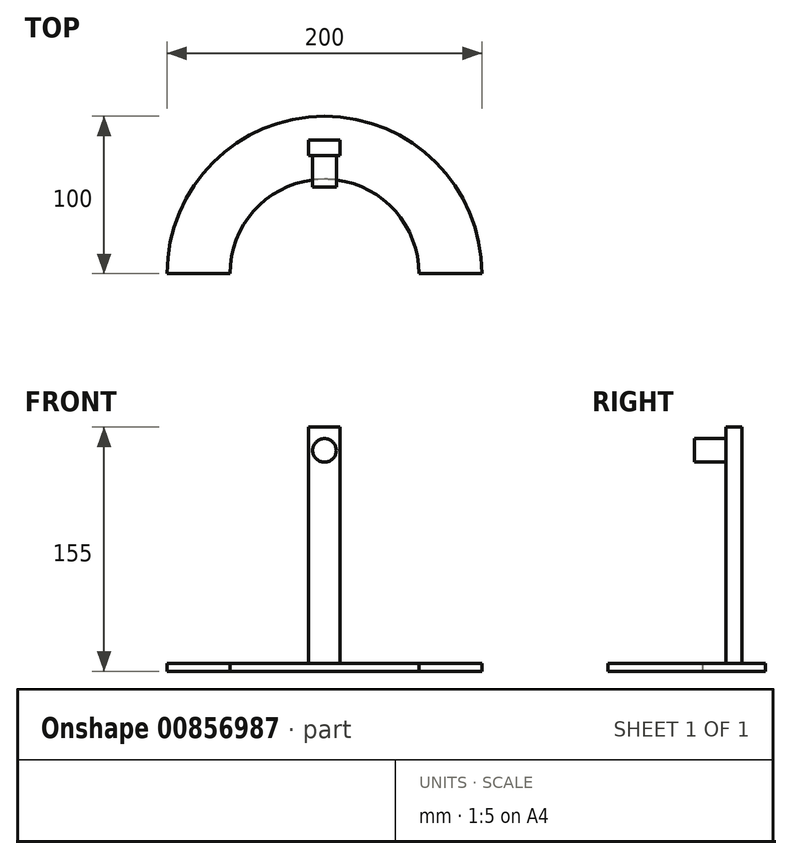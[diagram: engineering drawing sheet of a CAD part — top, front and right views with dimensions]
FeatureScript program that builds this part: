
annotation { "Feature Type Name" : "Feature", "Feature Type Description" : "" }
export const myFeature = defineFeature(function(context is Context, id is Id, definition is map)
    precondition{}
    {
        {
            var Q0;
            Q0=qCreatedBy(makeId("Top.planeOp"),FACE);
            var sketch = newSketch(context, id + "F0", { "sketchPlane" : qUnion([Q0])});
            skArc(sketch, "E0", {"start": v(100, 0) * mm, "mid": v(0, 100) * mm, "end": v(-100, 0) * mm});
            skLineSegment(sketch, "E1", {"start": v(-100, 0) * mm, "end": v(-60, 0) * mm});
            skPoint(sketch, "E2.orphan", {"position": v(-105.17, 0) * mm});
            skArc(sketch, "E3", {"start": v(60, 0) * mm, "mid": v(0, 60) * mm, "end": v(-60, 0) * mm});
            skLineSegment(sketch, "E4.trimOffspring", {"start": v(60, 0) * mm, "end": v(100, 0) * mm});
            skSolve(sketch);
        }
        {
            var Q0;
            Q0=makeQuery(id+"F0.imprint","IMPRINT",FACE,{"disambiguationData":[TD([[makeQuery(id+"F0.imprint","IMPRINT",EDGE,{"derivedFrom":sQuery(id+"F0.wireOp",EDGE,"E0")}),1.0]])]});
            extrude(context, id + "F1", {"entities" : qUnion([Q0]), "depth" : 5 * mm, "offsetDistance" : 25 * mm});
        }
        {
            var Q0;
            Q0=makeQuery(id+"F1.opExtrude","CAP_FACE",FACE,{"disambiguationData":[OSD([sQuery(id+"F0.wireOp",EDGE,"E0"),sQuery(id+"F0.wireOp",EDGE,"E1"),sQuery(id+"F0.wireOp",EDGE,"E3"),sQuery(id+"F0.wireOp",EDGE,"E4.trimOffspring")])],"isStart":false});
            var sketch = newSketch(context, id + "F2", { "sketchPlane" : qUnion([Q0])});
            skLineSegment(sketch, "E5.bottom", {"start": v(10, 75) * mm, "end": v(-10, 75) * mm});
            skLineSegment(sketch, "E5.top", {"start": v(10, 85) * mm, "end": v(-10, 85) * mm});
            skLineSegment(sketch, "E5.left", {"start": v(10, 75) * mm, "end": v(10, 85) * mm});
            skLineSegment(sketch, "E5.right", {"start": v(-10, 75) * mm, "end": v(-10, 85) * mm});
            skPoint(sketch, "E5.middle", {"position": v(0, 80) * mm});
            skSolve(sketch);
        }
        {
            var Q0;
            Q0=makeQuery(id+"F2.imprint","IMPRINT",FACE,{"disambiguationData":[TD([[makeQuery(id+"F2.imprint","IMPRINT",EDGE,{"derivedFrom":sQuery(id+"F2.wireOp",EDGE,"E5.bottom")}),-1.0]])]});
            extrude(context, id + "F3", {"entities" : qUnion([Q0]), "operationType" : NewBodyOperationType.ADD, "depth" : 150 * mm, "offsetDistance" : 25 * mm});
        }
        {
            var Q0;
            Q0=makeQuery(id+"F3.opExtrude","SWEPT_FACE",FACE,{"disambiguationData":[OSD([sQuery(id+"F2.wireOp",EDGE,"E5.bottom")])]});
            var sketch = newSketch(context, id + "F4", { "sketchPlane" : qUnion([Q0])});
            skCircle(sketch, "E6", {"center": v(0, 140.28) * mm, "radius": 7.5 * mm});
            skPoint(sketch, "E6.centerSnap0", {"position": v(0, 155) * mm});
            skSolve(sketch);
        }
        {
            var Q0;
            Q0 = qSketchRegion(id + "F4", true);
            extrude(context, id + "F5", {"entities" : qUnion([Q0]), "depth" : 20 * mm, "offsetDistance" : 25 * mm});
        }
    });
